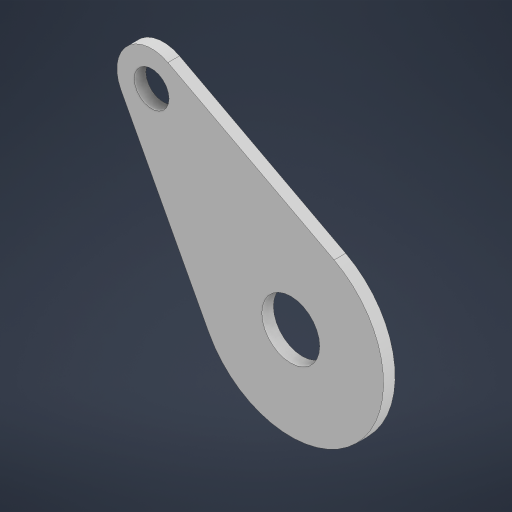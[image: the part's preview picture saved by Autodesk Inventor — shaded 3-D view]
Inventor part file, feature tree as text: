
AUTODESK INVENTOR PART (.ipt)
format: ipt  version: 2024 (Build 280153000, 153)  size: 194,048 bytes
history: native  units: in
note: dims shown in document units (in); Inventor stores cm internally (conversion verified against a paired STEP export)
features: extrude x1, sketch x1
ambient origin geometry x8: Origin, YZ Plane, XZ Plane, XY Plane, X Axis, Y Axis, Z Axis, Center Point
bodies: Solid1 (feature_tree)
feature tree (2):
  extrude  "Extrusion1"  Depth=0.0625in
  sketch  "Sketch1"  dims[d0=0.75in d1=0.75in d2=0.1875in d3=0.3125in d4=0.375in d5=1.0in d6=0.0625in d7=0.0in]
